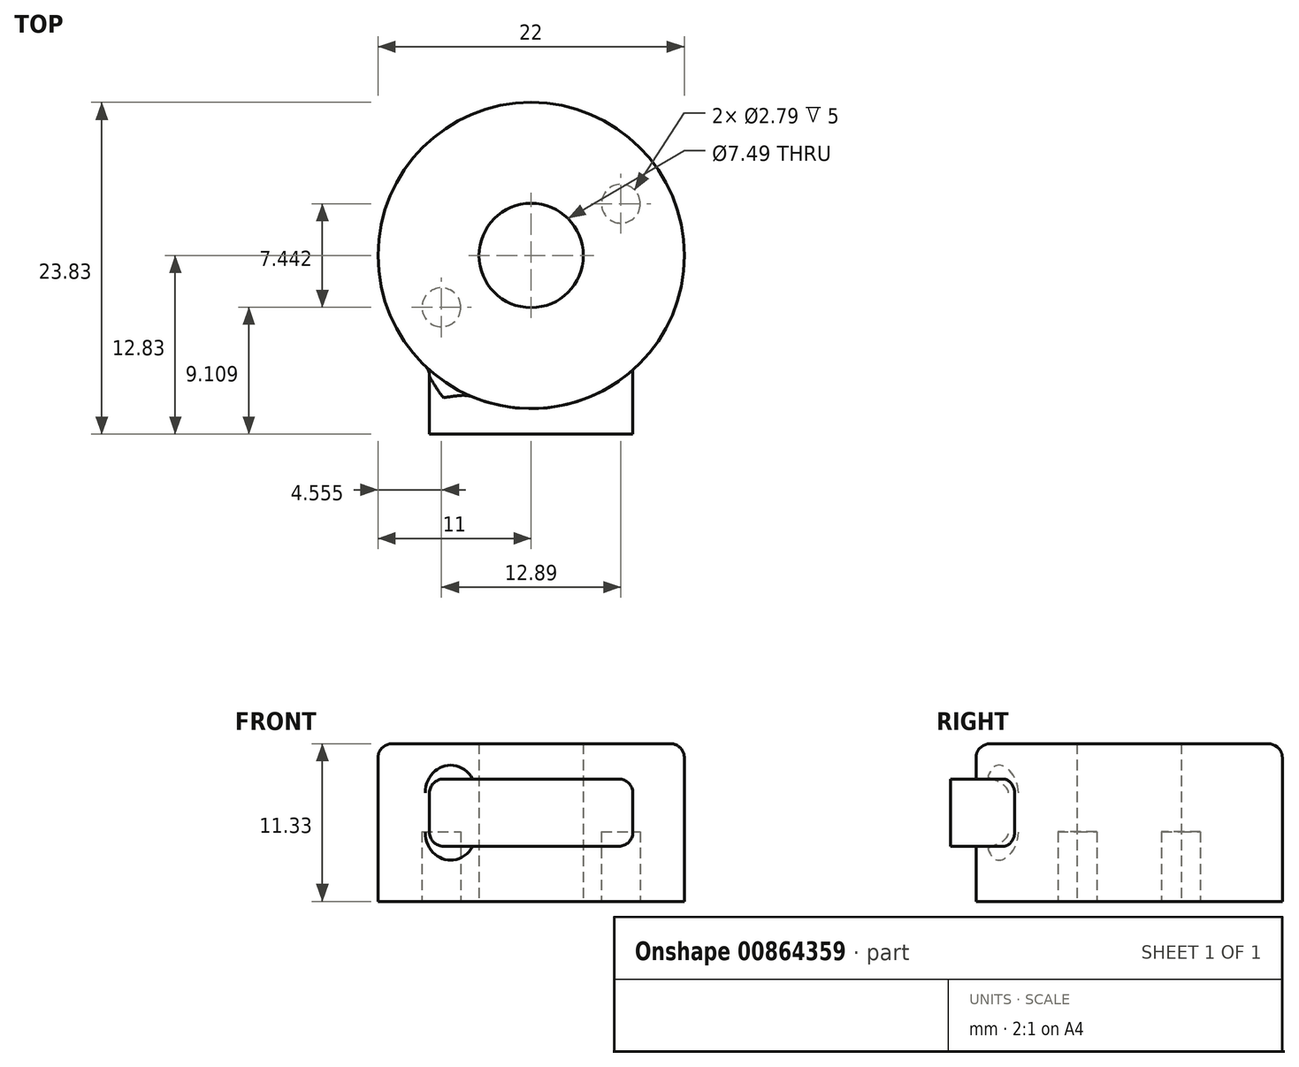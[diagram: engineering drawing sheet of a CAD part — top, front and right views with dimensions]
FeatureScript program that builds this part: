
annotation { "Feature Type Name" : "Feature", "Feature Type Description" : "" }
export const myFeature = defineFeature(function(context is Context, id is Id, definition is map)
    precondition{}
    {
        {
            var Q0;
            Q0=qCreatedBy(makeId("Top.planeOp"),FACE);
            var sketch = newSketch(context, id + "F0", { "sketchPlane" : qUnion([Q0])});
            skCircle(sketch, "E0", {"center": v(0, 0) * mm, "radius": 11 * mm});
            skSolve(sketch);
        }
        {
            var Q0;
            Q0 = qSketchRegion(id + "F0", true);
            extrude(context, id + "F1", {"entities" : qUnion([Q0]), "depth" : 11.33 * mm, "offsetDistance" : 25 * mm});
        }
        {
            var Q0;
            Q0=qCreatedBy(makeId("Front.planeOp"),FACE);
            var sketch = newSketch(context, id + "F2", { "sketchPlane" : qUnion([Q0])});
            skLineSegment(sketch, "E1.bottom", {"start": v(-7.3, 8.79) * mm, "end": v(7.3, 8.79) * mm});
            skLineSegment(sketch, "E1.top", {"start": v(-7.3, 3.96) * mm, "end": v(7.3, 3.96) * mm});
            skLineSegment(sketch, "E1.left", {"start": v(-7.3, 8.79) * mm, "end": v(-7.3, 3.96) * mm});
            skLineSegment(sketch, "E1.right", {"start": v(7.3, 8.79) * mm, "end": v(7.3, 3.96) * mm});
            skLineSegment(sketch, "E2", {"start": v(0, 0) * mm, "end": v(0, 3.96) * mm, "construction": true});
            skSolve(sketch);
        }
        {
            var Q0;
            Q0 = qSketchRegion(id + "F2", true);
            extrude(context, id + "F3", {"entities" : qUnion([Q0]), "operationType" : NewBodyOperationType.ADD, "depth" : 12.83 * mm, "offsetDistance" : 25 * mm});
        }
        {
            var Q0;
            Q0=makeQuery(id+"F1.opExtrude","CAP_EDGE",EDGE,{"disambiguationData":[OSD([sQuery(id+"F0.wireOp",EDGE,"E0")])],"isStart":false});
            var Q1;
            Q1=makeQuery(id+"F3.opExtrude","SWEPT_EDGE",EDGE,{"disambiguationData":[OSD([sQuery(id+"F2.wireOp",EDGE,"E1.bottom"),sQuery(id+"F2.wireOp",EDGE,"E1.right")])]});
            var Q2;
            Q2=makeQuery(id+"F3.opExtrude","SWEPT_EDGE",EDGE,{"disambiguationData":[OSD([sQuery(id+"F2.wireOp",EDGE,"E1.top"),sQuery(id+"F2.wireOp",EDGE,"E1.right")])]});
            var Q3;
            Q3=makeQuery(id+"F3.opExtrude","SWEPT_EDGE",EDGE,{"disambiguationData":[OSD([sQuery(id+"F2.wireOp",EDGE,"E1.bottom"),sQuery(id+"F2.wireOp",EDGE,"E1.left")])]});
            var Q4;
            Q4=makeQuery(id+"F3.opExtrude","SWEPT_EDGE",EDGE,{"disambiguationData":[OSD([sQuery(id+"F2.wireOp",EDGE,"E1.top"),sQuery(id+"F2.wireOp",EDGE,"E1.left")])]});
            var Q5;
            Q5=makeQuery(id+"F3.boolean.opBoolean","INTERSECT",EDGE,{"derivedFrom":[makeQuery(id+"F1.opExtrude","SWEPT_FACE",FACE,{"disambiguationData":[OSD([sQuery(id+"F0.wireOp",EDGE,"E0")])]}),makeQuery(id+"F3.opExtrude","SWEPT_FACE",FACE,{"disambiguationData":[OSD([sQuery(id+"F2.wireOp",EDGE,"E1.left")])]})]});
            fillet(context, id + "F4", {"entities" : qUnion([Q0, Q1, Q2, Q3, Q4, Q5]), "radius" : 1 * mm, "tangentPropagation" : true, "allowEdgeOverflow" : false});
        }
        {
            var Q0;
            Q0=makeQuery(id+"F1.opExtrude","CAP_FACE",FACE,{"disambiguationData":[OSD([sQuery(id+"F0.wireOp",EDGE,"E0")])],"isStart":true});
            var sketch = newSketch(context, id + "F5", { "sketchPlane" : qUnion([Q0])});
            skCircle(sketch, "E3", {"center": v(0, 0) * mm, "radius": 3.75 * mm});
            skSolve(sketch);
        }
        {
            var Q0;
            Q0 = qSketchRegion(id + "F5", true);
            extrude(context, id + "F6", {"entities" : qUnion([Q0]), "operationType" : NewBodyOperationType.REMOVE, "endBound" : BoundingType.THROUGH_ALL, "oppositeDirection" : true, "depth" : 25 * mm, "offsetDistance" : 25 * mm});
        }
        {
            var Q0;
            Q0=makeQuery(id+"F1.opExtrude","CAP_FACE",FACE,{"disambiguationData":[OSD([sQuery(id+"F0.wireOp",EDGE,"E0")])],"isStart":true});
            var sketch = newSketch(context, id + "F7", { "sketchPlane" : qUnion([Q0])});
            skLineSegment(sketch, "E4", {"start": v(6.45, -3.72) * mm, "end": v(-6.45, 3.72) * mm, "construction": true});
            skLineSegment(sketch, "E5", {"start": v(0, 0) * mm, "end": v(0, 11) * mm, "construction": true});
            skCircle(sketch, "E6", {"center": v(-6.45, 3.72) * mm, "radius": 1.4 * mm});
            skCircle(sketch, "E7", {"center": v(6.45, -3.72) * mm, "radius": 1.4 * mm});
            skSolve(sketch);
        }
        {
            var Q0;
            Q0 = qSketchRegion(id + "F7", true);
            extrude(context, id + "F8", {"entities" : qUnion([Q0]), "operationType" : NewBodyOperationType.REMOVE, "oppositeDirection" : true, "depth" : 5 * mm, "offsetDistance" : 25 * mm});
        }
    });
